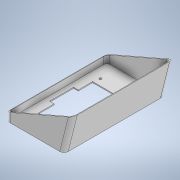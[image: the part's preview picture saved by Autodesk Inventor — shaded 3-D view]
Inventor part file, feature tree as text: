
AUTODESK INVENTOR PART (.ipt)
format: ipt  version: 2022 (Build 260153000, 153)  size: 242,176 bytes
history: native  units: mm
features: extrude x6, sketch x6, fillet x1, plane x1, projected_geometry x1
ambient origin geometry x8: Origin, YZ Plane, XZ Plane, XY Plane, X Axis, Y Axis, Z Axis, Center Point
bodies: Solid1 (feature_tree)
feature tree (15):
  extrude  "Extrusion1"  Depth=193.2mm
  extrude  "Extrusion3"  Depth=4.2mm
  extrude  "Extrusion4"  Depth=65.697mm
  extrude  "Extrusion5"  Depth=4.2mm
  extrude  "Extrusion6"  Depth=126.501mm
  fillet  "Fillet1"  [1 undecoded]
  plane  "Work Plane1"
  extrude  "Extrusion7"  Depth=193.2mm
  sketch  "Sketch1"  dims[d0=110.94mm d1=193.2mm]
  sketch  "Sketch3"  dims[d2=4.2mm d3=4.2mm]
  sketch  "Sketch4"  dims[d4=65.3mm d5=65.697mm]
  projected_geometry  "Projected Loop2"
  sketch  "Sketch5"  dims[d6=4.2mm d7=4.2mm]
  sketch  "Sketch6"  dims[d8=126.2mm d9=126.501mm d10=0.0mm]
  sketch  "Sketch9"  dims[d11=22.6mm d12=35.0mm d13=8.0mm d14=2.0mm d15=0.0mm d22=105.0mm d23=79.0mm d26=40.0mm d27=40.0mm d29=7.5mm d30=0.0mm d32=12.0mm d33=41.0mm d34=11.0mm d35=79.0mm d36=79.0mm d37=2.0mm d38=60.0mm d39=0.0mm d40=14.0mm d41=0.0mm d42=1000.0mm d43=0.0mm d47=140.0mm d48=193.2mm d49=0.0mm d50=8.0mm d54=90.0deg d55=2.0mm d56=8.0mm d57=193.2mm d58=0.0mm]
note: 1 required parameter value undecoded (feature->parameter linkage not recoverable at this tier; creation-order binding heuristic only, values carry confidence <= 0.55)
